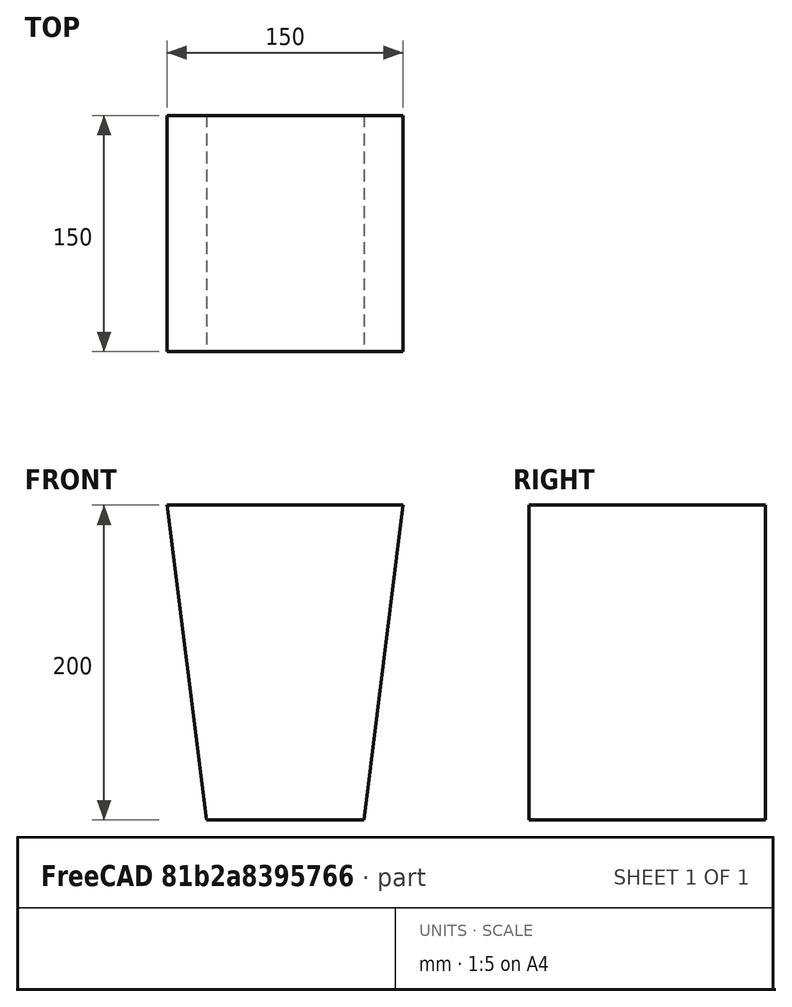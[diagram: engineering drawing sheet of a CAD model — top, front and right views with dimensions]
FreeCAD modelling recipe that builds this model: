
FCSTD DOCUMENT  (FreeCAD 0.15R4671 (Git))
Label: ermina_v3
License: All rights reserved
LicenseURL: http://en.wikipedia.org/wiki/All_rights_reserved
objects: Sketcher::SketchObject×3, PartDesign::Pad×1
note: 5 computed .brp shape members not serialized (recipe doc carries the construction recipe); baked Part::Feature solids carry a one-line shape summary decoded from their .brp

FEATURE [Sketcher::SketchObject] Sketch
  Placement = pos=(0,0,0) rot=(-1,0,0;4.71239rad)
  sketch-geometry (4):
    g0: LineSegment StartX=-50 StartY=0 StartZ=0 EndX=50 EndY=0 EndZ=0
    g1: LineSegment StartX=50 StartY=0 StartZ=0 EndX=75 EndY=200 EndZ=0
    g2: LineSegment StartX=75 StartY=200 StartZ=0 EndX=-75 EndY=200 EndZ=0
    g3: LineSegment StartX=-75 StartY=200 StartZ=0 EndX=-50 EndY=0 EndZ=0
  constraints (10):
    c: Horizontal(g0)
    c: Coincident(g1,g2)
    c: Horizontal(g2)
    c: Coincident(g2,g3)
    c: DistanceX(g0) = 100
    c: DistanceX(g2) = -150
    c: PointOnObject(g0,g-1)
    c: Distance(g2,g0) = 200
    c: Equal(g1,g3)
    c: DistanceX(g-2,g1) = 75
FEATURE [PartDesign::Pad] Pad
  Length = 150
  Length2 = 100
  Placement = pos=(0,0,0) rot=(-1,0,0;4.71239rad)
  Sketch = -> Sketch
  Type = 0
FEATURE [Sketcher::SketchObject] Sketch001
  Placement = pos=(0,0,0) rot=(-1,0,0;1.5708rad)
  Support = -> Pad [Face5]
FEATURE [Sketcher::SketchObject] Sketch002
  ExternalGeometry = -> [Pad]
  Placement = pos=(0,-150,0) rot=(1,0,0;1.5708rad)
  Support = -> Pad [Face6]
  sketch-geometry (4):
    g0: LineSegment StartX=66.25 StartY=130 StartZ=0 EndX=162.5 EndY=100 EndZ=0
    g1: LineSegment StartX=162.5 StartY=100 StartZ=0 EndX=192.5 EndY=0 EndZ=0
    g2: LineSegment StartX=66.25 StartY=130 StartZ=0 EndX=50 EndY=0 EndZ=0
    g3: LineSegment StartX=50 StartY=0 StartZ=0 EndX=192.5 EndY=0 EndZ=0
  constraints (7):
    c: Coincident(g0,g1)
    c: PointOnObject(g1,g-1)
    c: Coincident(g2,g0)
    c: Coincident(g3,g2)
    c: Coincident(g3,g1)
    c: Horizontal(g3)
    c: PointOnObject(g0,g-4)
